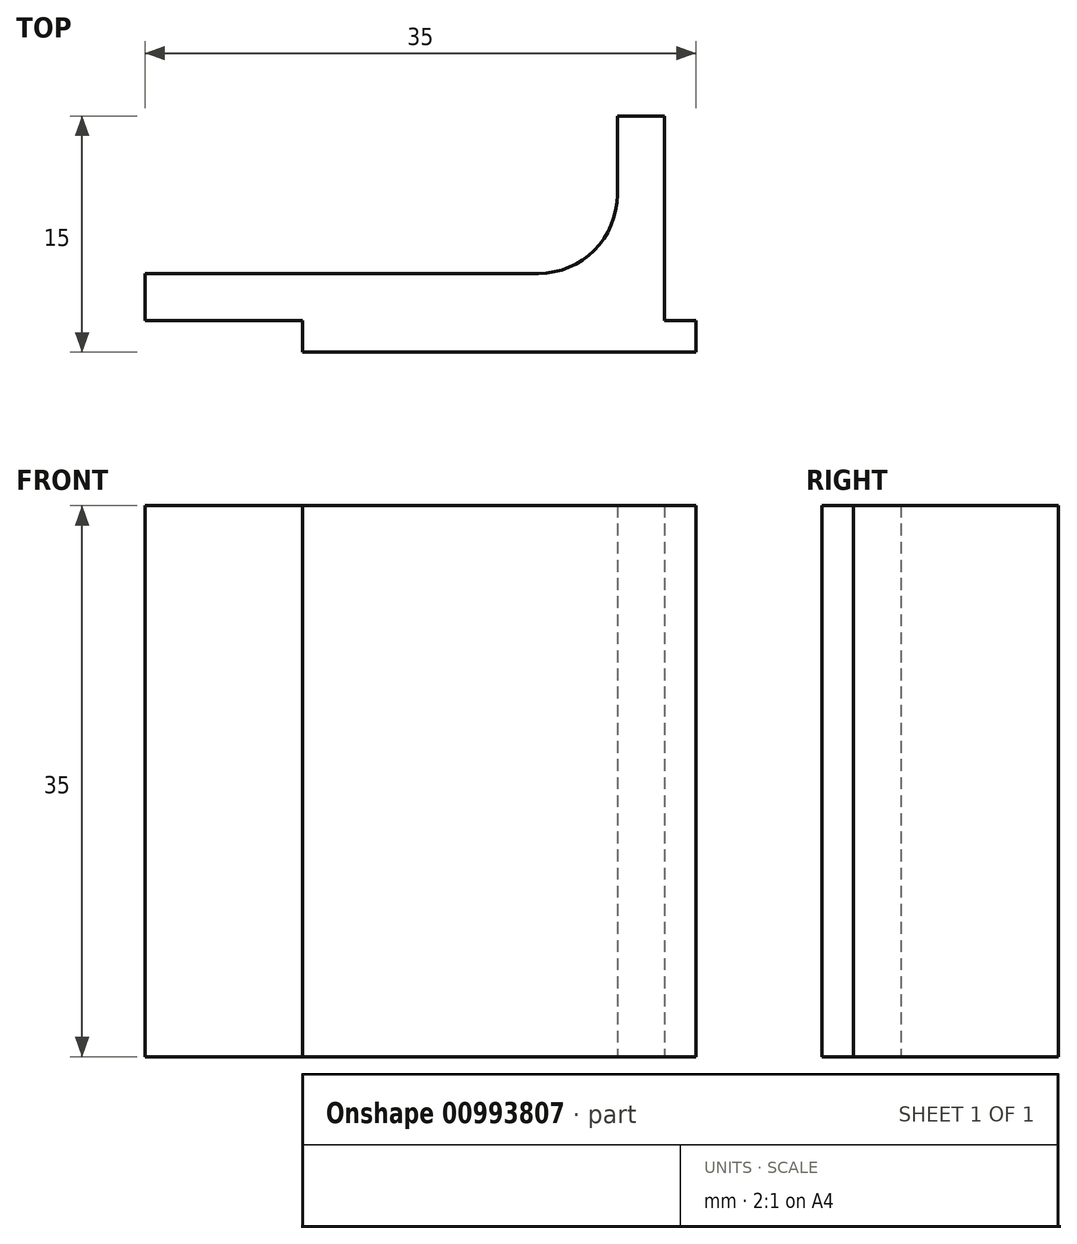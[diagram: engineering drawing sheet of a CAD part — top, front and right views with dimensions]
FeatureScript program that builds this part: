
annotation { "Feature Type Name" : "Feature", "Feature Type Description" : "" }
export const myFeature = defineFeature(function(context is Context, id is Id, definition is map)
    precondition{}
    {
        {
            var Q0;
            Q0=qCreatedBy(makeId("Top.planeOp"),FACE);
            var sketch = newSketch(context, id + "F0", { "sketchPlane" : qUnion([Q0])});
            skLineSegment(sketch, "E0", {"start": v(-36.8, 3) * mm, "end": v(-6.8, 3) * mm});
            skLineSegment(sketch, "E1", {"start": v(-6.8, 3) * mm, "end": v(-6.8, 13) * mm});
            skLineSegment(sketch, "E2", {"start": v(-6.8, 13) * mm, "end": v(-3.8, 13) * mm});
            skLineSegment(sketch, "E3", {"start": v(-3.8, 13) * mm, "end": v(-3.8, 0) * mm});
            skLineSegment(sketch, "E4", {"start": v(-3.8, -2) * mm, "end": v(-26.8, -2) * mm});
            skLineSegment(sketch, "E5", {"start": v(-26.8, -2) * mm, "end": v(-26.8, 0) * mm});
            skLineSegment(sketch, "E6", {"start": v(-26.8, 0) * mm, "end": v(-36.8, 0) * mm});
            skLineSegment(sketch, "E7", {"start": v(-36.8, 0) * mm, "end": v(-36.8, 3) * mm});
            skLineSegment(sketch, "E8", {"start": v(-3.8, 0) * mm, "end": v(-1.8, 0) * mm});
            skLineSegment(sketch, "E9", {"start": v(-1.8, 0) * mm, "end": v(-1.8, -2) * mm});
            skLineSegment(sketch, "E10", {"start": v(-1.8, -2) * mm, "end": v(-3.8, -2) * mm});
            skSolve(sketch);
        }
        {
            var Q0;
            Q0 = qSketchRegion(id + "F0", true);
            extrude(context, id + "F1", {"entities" : qUnion([Q0]), "depth" : 35 * mm, "offsetDistance" : 25 * mm, "symmetric" : true});
        }
        {
            var Q0;
            Q0=makeQuery(id+"F1.opExtrude","SWEPT_EDGE",EDGE,{"disambiguationData":[OSD([sQuery(id+"F0.wireOp",EDGE,"E0"),sQuery(id+"F0.wireOp",EDGE,"E1")])]});
            fillet(context, id + "F2", {"entities" : qUnion([Q0]), "tangentPropagation" : true, "radius" : 5 * mm, "defaultsChanged" : false, "vertexSettings" : [], "allowEdgeOverflow" : false});
        }
    });
